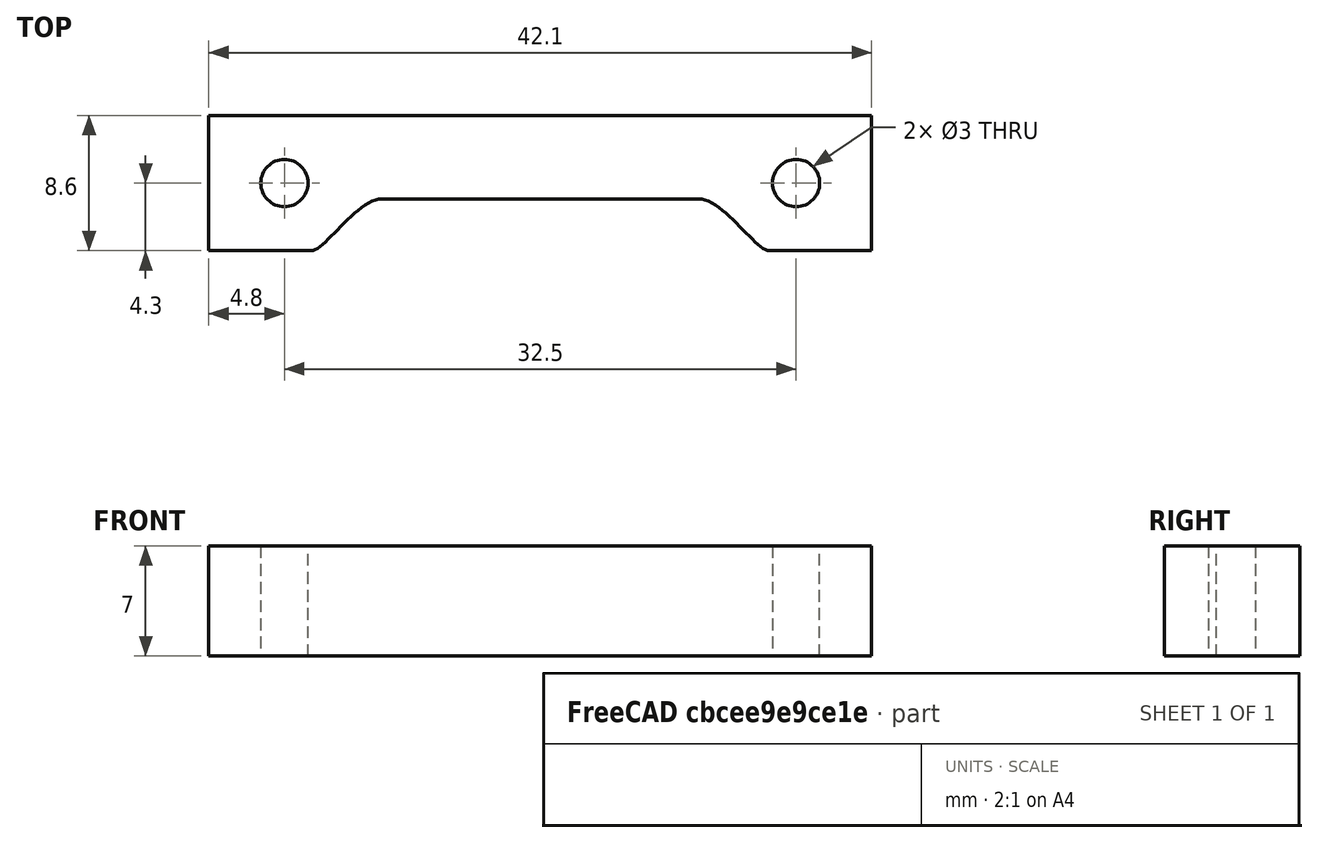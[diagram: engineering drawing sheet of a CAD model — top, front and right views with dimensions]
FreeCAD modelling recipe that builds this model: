
FCSTD DOCUMENT  (FreeCAD 0.19R0.19.2)
Label: 004
License: All rights reserved
LicenseURL: http://en.wikipedia.org/wiki/All_rights_reserved
objects: Sketcher::SketchObject×2, Part::Extrusion×1
note: 3 computed .brp shape members not serialized (recipe doc carries the construction recipe); baked Part::Feature solids carry a one-line shape summary decoded from their .brp

FEATURE [Sketcher::SketchObject] Sketch  label="attatchmentPiece"
  FullyConstrained = true
  sketch-geometry (28):
    g0: Circle CenterX=-16.25 CenterY=0 CenterZ=0 NormalX=0 NormalY=0 NormalZ=1 AngleXU=0 Radius=1.5
    g1: Circle CenterX=16.25 CenterY=0 CenterZ=0 NormalX=0 NormalY=0 NormalZ=1 AngleXU=0 Radius=1.5
    g2: LineSegment StartX=21.05 StartY=0 StartZ=0 EndX=21.05 EndY=-1 EndZ=0
    g3: LineSegment StartX=21.05 StartY=-1 StartZ=0 EndX=21.05 EndY=-4.3 EndZ=0
    g4: LineSegment StartX=-21.05 StartY=0 StartZ=0 EndX=-21.05 EndY=-1 EndZ=0
    g5: LineSegment StartX=-21.05 StartY=-1 StartZ=0 EndX=-21.05 EndY=-4.3 EndZ=0
    g6: LineSegment StartX=-21.05 StartY=-4.3 StartZ=0 EndX=-16.25 EndY=-4.3 EndZ=0
    g7: LineSegment StartX=-16.25 StartY=4.3 StartZ=0 EndX=21.05 EndY=4.3 EndZ=0
    g8: LineSegment StartX=-16.25 StartY=4.3 StartZ=0 EndX=-21.05 EndY=4.3 EndZ=0
    g9: LineSegment StartX=-21.05 StartY=0 StartZ=0 EndX=-21.05 EndY=4.3 EndZ=0
    g10: LineSegment StartX=21.05 StartY=0 StartZ=0 EndX=21.05 EndY=4.3 EndZ=0
    g11-g14: Circle x4 (B-spline internal-alignment scaffolding for g15; pole/knot coordinates omitted)
    g15: BSplineCurve PolesCount=4 KnotsCount=2 Degree=3 IsPeriodic=0
    g16: GeomPoint X=-10.05 Y=-1 Z=0
    g17: GeomPoint X=-14.55 Y=-4.3 Z=0
    g18-g21: Circle x4 (B-spline internal-alignment scaffolding for g22; pole/knot coordinates omitted)
    g22: BSplineCurve PolesCount=4 KnotsCount=2 Degree=3 IsPeriodic=0
    g23: GeomPoint X=10.05 Y=-1 Z=0
    g24: GeomPoint X=14.55 Y=-4.3 Z=0
    g25: LineSegment StartX=10.05 StartY=-1 StartZ=0 EndX=-10.05 EndY=-1 EndZ=0
    g26: LineSegment StartX=-16.25 StartY=-4.3 StartZ=0 EndX=-14.55 EndY=-4.3 EndZ=0
    g27: LineSegment StartX=14.55 StartY=-4.3 StartZ=0 EndX=21.05 EndY=-4.3 EndZ=0
  constraints (49):
    c: Block(g1)
    c: Block(g0)
    c: Vertical(g2)
    c: Coincident(g3,g2)
    c: Vertical(g3)
    c: Block(g2)
    c: Vertical(g4)
    c: Block(g4)
    c: Vertical(g5)
    c: Coincident(g5,g4)
    c: Distance(g5) = 3.3
    c: Horizontal(g6)
    c: Coincident(g6,g5)
    c: Distance(g6) = 4.8
    c: Horizontal(g7)
    c: Horizontal(g8)
    c: Vertical(g9)
    c: Coincident(g9,g8)
    c: Vertical(g10)
    c: Coincident(g10,g7)
    c: Block(g7)
    c: Block(g9)
    c: Block(g8)
    c: Block(g10)
    c: Weight(g11) = 1
    c: Equal(g11,g12)
    c: Equal(g11,g13)
    c: Equal(g11,g14)
    c: InternalAlignment(g11-g14 -> g15) x4
    c: InternalAlignment(g16,g15)
    c: InternalAlignment(g17,g15)
    c: Weight(g18) = 1
    c: Equal(g18,g19)
    c: Equal(g18,g20)
    c: Equal(g18,g21)
    c: InternalAlignment(g18-g21 -> g22) x4
    c: InternalAlignment(g23,g22)
    c: InternalAlignment(g24,g22)
    c: Block(g22)
    c: Block(g15)
    c: Coincident(g25,g22)
    c: Coincident(g25,g15)
    c: Horizontal(g25)
    c: Coincident(g26,g6)
    c: Coincident(g26,g15)
    c: Horizontal(g26)
    c: Coincident(g27,g22)
    c: Coincident(g27,g3)
    c: Horizontal(g27)
FEATURE [Part::Extrusion] Extrude  label="attatchmentPiece001"
  Base = -> Sketch
  Dir = (0,0,1)
  DirMode = 2
  FaceMakerClass = Part::FaceMakerBullseye
  LengthFwd = 7
  LengthRev = 0
  Solid = true
  Symmetric = false
FEATURE [Sketcher::SketchObject] Sketch001  label="attatchmentPieceSurround"
  FullyConstrained = true
  sketch-geometry (22):
    g0: LineSegment StartX=-21.05 StartY=-4.3 StartZ=0 EndX=-25.85 EndY=-4.3 EndZ=0
    g1: LineSegment StartX=25.85 StartY=-4.3 StartZ=0 EndX=21.05 EndY=-4.3 EndZ=0
    g2: LineSegment StartX=-25.85 StartY=-4.3 StartZ=0 EndX=-25.85 EndY=4.3 EndZ=0
    g3: LineSegment StartX=25.85 StartY=-4.3 StartZ=0 EndX=25.85 EndY=4.3 EndZ=0
    g4: LineSegment StartX=-21.05 StartY=8.9 StartZ=0 EndX=21.05 EndY=8.9 EndZ=0
    g5: Circle CenterX=-21.05 CenterY=8.9 CenterZ=0 NormalX=0 NormalY=0 NormalZ=1 AngleXU=0 Radius=1
    g6: Circle CenterX=-25.85 CenterY=8.9 CenterZ=0 NormalX=0 NormalY=0 NormalZ=1 AngleXU=0 Radius=1
    g7: Circle CenterX=-25.85 CenterY=4.3 CenterZ=0 NormalX=0 NormalY=0 NormalZ=1 AngleXU=0 Radius=1
    g8: BSplineCurve PolesCount=3 KnotsCount=2 Degree=2 IsPeriodic=0
    g9: GeomPoint X=-21.05 Y=8.9 Z=0
    g10: GeomPoint X=-25.85 Y=4.3 Z=0
    g11: Circle CenterX=21.05 CenterY=8.9 CenterZ=0 NormalX=0 NormalY=0 NormalZ=1 AngleXU=0 Radius=1
    g12: Circle CenterX=25.85 CenterY=8.9 CenterZ=0 NormalX=0 NormalY=0 NormalZ=1 AngleXU=0 Radius=1
    g13: Circle CenterX=25.85 CenterY=4.3 CenterZ=0 NormalX=0 NormalY=0 NormalZ=1 AngleXU=0 Radius=1
    g14: BSplineCurve PolesCount=3 KnotsCount=2 Degree=2 IsPeriodic=0
    g15: GeomPoint X=21.05 Y=8.9 Z=0
    g16: GeomPoint X=25.85 Y=4.3 Z=0
    g17: ArcOfCircle CenterX=-19.45 CenterY=2.7 CenterZ=0 NormalX=0 NormalY=0 NormalZ=1 AngleXU=0 Radius=1.6 StartAngle=1.5708 EndAngle=3.14159
    g18: ArcOfCircle CenterX=19.45 CenterY=2.7 CenterZ=0 NormalX=0 NormalY=0 NormalZ=1 AngleXU=0 Radius=1.6 StartAngle=0 EndAngle=1.5708
    g19: LineSegment StartX=-19.45 StartY=4.3 StartZ=0 EndX=19.45 EndY=4.3 EndZ=0
    g20: LineSegment StartX=21.05 StartY=2.7 StartZ=0 EndX=21.05 EndY=-4.3 EndZ=0
    g21: LineSegment StartX=-21.05 StartY=2.7 StartZ=0 EndX=-21.05 EndY=-4.3 EndZ=0
  constraints (48):
    c: Horizontal(g0)
    c: Distance(g0) = 4.8
    c: Horizontal(g1)
    c: Equal(g0,g1) = 4.8
    c: Coincident(g2,g0)
    c: Vertical(g2)
    c: Distance(g2) = 8.6
    c: Vertical(g3)
    c: Equal(g2,g3) = 8.6
    c: Coincident(g3,g1)
    c: Horizontal(g4)
    c: Distance(g4) = 42.1
    c: Block(g4)
    c: Coincident(g8,g4)
    c: Weight(g5) = 1
    c: Equal(g5,g6)
    c: Equal(g5,g7)
    c: Coincident(g8,g2)
    c: InternalAlignment(g5,g8)
    c: InternalAlignment(g6,g8)
    c: InternalAlignment(g7,g8)
    c: InternalAlignment(g9,g8)
    c: InternalAlignment(g10,g8)
    c: Coincident(g14,g4)
    c: Weight(g11) = 1
    c: Equal(g11,g12)
    c: Equal(g11,g13)
    c: Coincident(g14,g3)
    c: InternalAlignment(g11,g14)
    c: InternalAlignment(g12,g14)
    c: InternalAlignment(g13,g14)
    c: InternalAlignment(g15,g14)
    c: InternalAlignment(g16,g14)
    c: Block(g1)
    c: Block(g2)
    c: Block(g14)
    c: Block(g8)
    c: Block(g18)
    c: Block(g17)
    c: Coincident(g19,g17)
    c: Coincident(g19,g18)
    c: Horizontal(g19)
    c: Coincident(g20,g18)
    c: Coincident(g20,g1)
    c: Vertical(g20)
    c: Coincident(g21,g17)
    c: Coincident(g21,g0)
    c: Vertical(g21)
